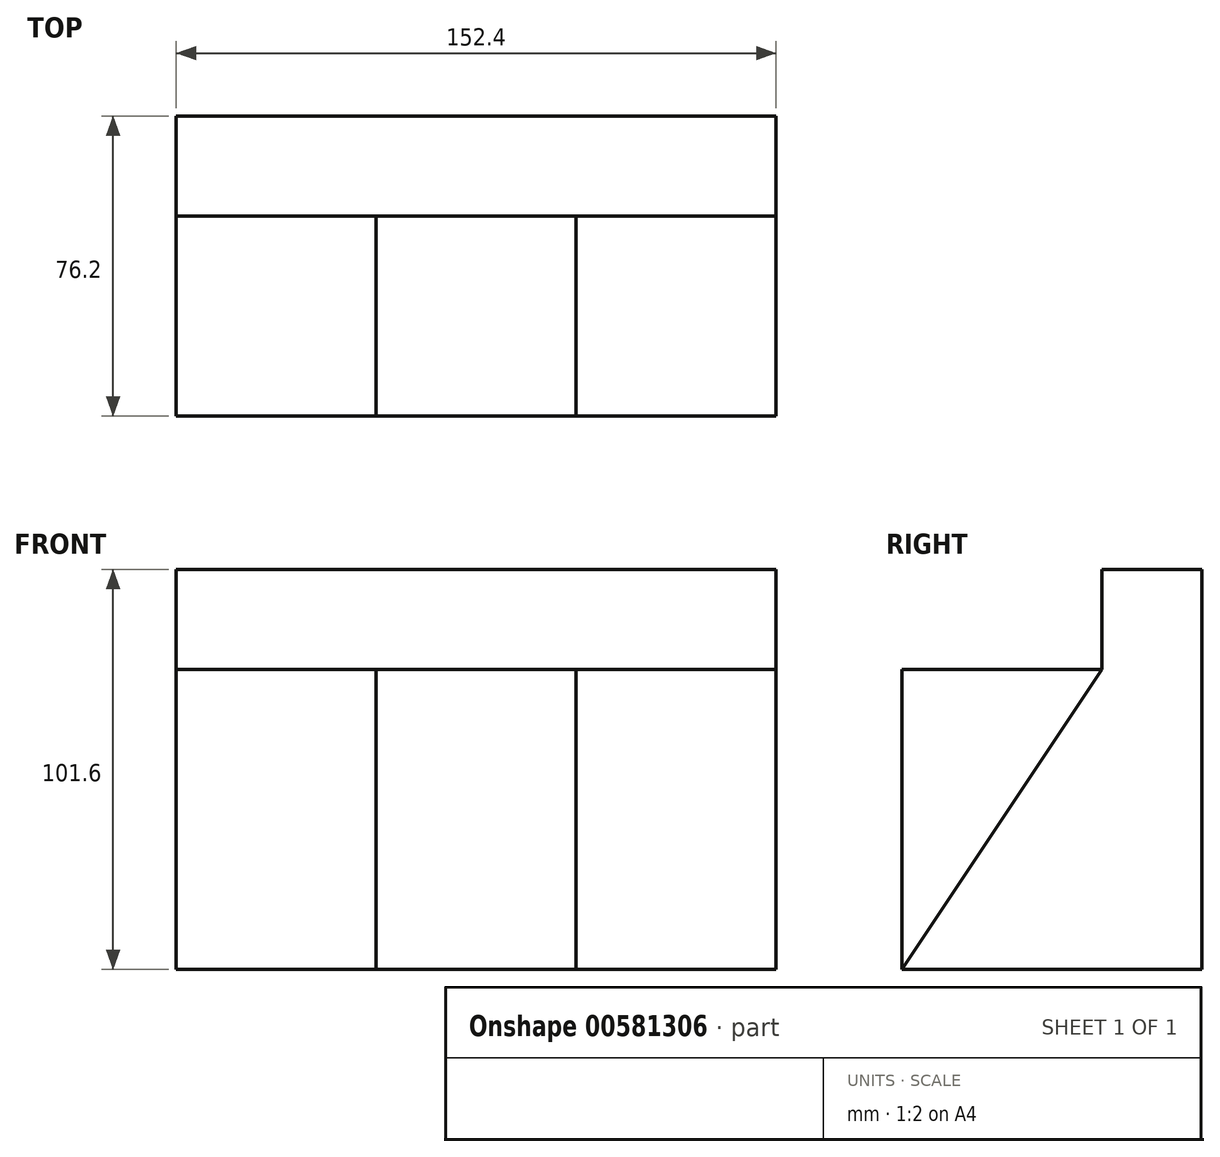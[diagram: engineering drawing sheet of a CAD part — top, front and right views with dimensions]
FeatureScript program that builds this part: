
annotation { "Feature Type Name" : "Feature", "Feature Type Description" : "" }
export const myFeature = defineFeature(function(context is Context, id is Id, definition is map)
    precondition{}
    {
        {
            var Q0;
            Q0=qCreatedBy(makeId("Top.planeOp"),FACE);
            var sketch = newSketch(context, id + "F0", { "sketchPlane" : qUnion([Q0])});
            skLineSegment(sketch, "E0.bottom", {"start": v(-69.4, 16.66) * mm, "end": v(83, 16.66) * mm});
            skLineSegment(sketch, "E0.top", {"start": v(-69.4, -59.54) * mm, "end": v(83, -59.54) * mm});
            skLineSegment(sketch, "E0.left", {"start": v(-69.4, 16.66) * mm, "end": v(-69.4, -59.54) * mm});
            skLineSegment(sketch, "E0.right", {"start": v(83, 16.66) * mm, "end": v(83, -59.54) * mm});
            skSolve(sketch);
        }
        {
            var Q0;
            Q0=makeQuery(id+"F0.imprint","IMPRINT",FACE,{"disambiguationData":[TD([[makeQuery(id+"F0.imprint","IMPRINT",EDGE,{"derivedFrom":sQuery(id+"F0.wireOp",EDGE,"E0.bottom")}),-1.0]])]});
            extrude(context, id + "F1", {"entities" : qUnion([Q0]), "depth" : 101.6 * mm, "offsetDistance" : 25.4 * mm});
        }
        {
            var Q0;
            Q0=makeQuery(id+"F1.opExtrude","SWEPT_FACE",FACE,{"disambiguationData":[OSD([sQuery(id+"F0.wireOp",EDGE,"E0.right")])]});
            var sketch = newSketch(context, id + "F2", { "sketchPlane" : qUnion([Q0])});
            skLineSegment(sketch, "E1.right", {"start": v(16.66, 76.2) * mm, "end": v(16.66, 0) * mm});
            skLineSegment(sketch, "E2.bottom", {"start": v(16.66, 76.2) * mm, "end": v(-8.74, 76.2) * mm});
            skLineSegment(sketch, "E2.top", {"start": v(16.66, 0) * mm, "end": v(-8.74, 0) * mm});
            skLineSegment(sketch, "E2.right", {"start": v(-8.74, 76.2) * mm, "end": v(-8.74, 0) * mm});
            skLineSegment(sketch, "E3", {"start": v(-8.74, 76.2) * mm, "end": v(-59.54, 0) * mm});
            skLineSegment(sketch, "E4.bottom", {"start": v(-8.74, 76.2) * mm, "end": v(16.66, 76.2) * mm});
            skLineSegment(sketch, "E4.top", {"start": v(-8.74, 101.6) * mm, "end": v(16.66, 101.6) * mm});
            skLineSegment(sketch, "E4.left", {"start": v(-8.74, 76.2) * mm, "end": v(-8.74, 101.6) * mm});
            skLineSegment(sketch, "E4.right", {"start": v(16.66, 76.2) * mm, "end": v(16.66, 101.6) * mm});
            skSolve(sketch);
        }
        {
            var Q0;
            Q0=makeQuery(id+"F1.opExtrude","SWEPT_FACE",FACE,{"disambiguationData":[OSD([sQuery(id+"F0.wireOp",EDGE,"E0.top")])]});
            var sketch = newSketch(context, id + "F3", { "sketchPlane" : qUnion([Q0])});
            skLineSegment(sketch, "E5.bottom", {"start": v(-69.4, 76.2) * mm, "end": v(-18.6, 76.2) * mm});
            skLineSegment(sketch, "E5.top", {"start": v(-69.4, 0) * mm, "end": v(-18.6, 0) * mm});
            skLineSegment(sketch, "E5.left", {"start": v(-69.4, 76.2) * mm, "end": v(-69.4, 0) * mm});
            skLineSegment(sketch, "E5.right", {"start": v(-18.6, 76.2) * mm, "end": v(-18.6, 0) * mm});
            skLineSegment(sketch, "E6.bottom", {"start": v(-18.6, 76.2) * mm, "end": v(32.2, 76.2) * mm});
            skLineSegment(sketch, "E6.top", {"start": v(-18.6, 0) * mm, "end": v(32.2, 0) * mm});
            skLineSegment(sketch, "E6.right", {"start": v(32.2, 76.2) * mm, "end": v(32.2, 0) * mm});
            skLineSegment(sketch, "E7.bottom", {"start": v(32.2, 76.2) * mm, "end": v(83, 76.2) * mm});
            skLineSegment(sketch, "E7.top", {"start": v(32.2, 0) * mm, "end": v(83, 0) * mm});
            skLineSegment(sketch, "E7.right", {"start": v(83, 76.2) * mm, "end": v(83, 0) * mm});
            skSolve(sketch);
        }
        {
            var Q0;
            {var subQ4=sQuery(id+"F3.wireOp",EDGE,"E5.bottom");Q0=makeQuery(id+"F3.imprint","IMPRINT",FACE,{"disambiguationData":[TD([[makeQuery(id+"F3.imprint","IMPRINT",EDGE,{"derivedFrom":subQ4}),1.0]])]});}
            extrude(context, id + "F4", {"entities" : qUnion([Q0]), "operationType" : NewBodyOperationType.REMOVE, "oppositeDirection" : true, "depth" : 50.8 * mm, "offsetDistance" : 25.4 * mm});
        }
        {
            var Q0;
            Q0=makeQuery(id+"F2.imprint","IMPRINT",FACE,{"disambiguationData":[TD([[makeQuery(id+"F2.imprint","IMPRINT",EDGE,{"derivedFrom":sQuery(id+"F2.wireOp",EDGE,"E3")}),-1.0]])]});
            extrude(context, id + "F5", {"entities" : qUnion([Q0]), "operationType" : NewBodyOperationType.REMOVE, "oppositeDirection" : true, "depth" : 50.8 * mm, "offsetDistance" : 25.4 * mm});
        }
        {
            var Q0;
            Q0=makeQuery(id+"F1.opExtrude","SWEPT_FACE",FACE,{"disambiguationData":[OSD([sQuery(id+"F0.wireOp",EDGE,"E0.left")])]});
            var sketch = newSketch(context, id + "F6", { "sketchPlane" : qUnion([Q0])});
            skLineSegment(sketch, "E8", {"start": v(8.74, 76.2) * mm, "end": v(59.54, 0) * mm});
            skSolve(sketch);
        }
        {
            var Q0;
            Q0=qSketchRegion(id+"F6",true);
            var Q1;
            Q1=makeQuery(id+"F6.imprint","IMPRINT",FACE,{"disambiguationData":[TD([[makeQuery(id+"F6.imprint","IMPRINT",EDGE,{"derivedFrom":sQuery(id+"F6.wireOp",EDGE,"E8")}),1.0]])]});
            extrude(context, id + "F7", {"entities" : qUnion([Q0, Q1]), "operationType" : NewBodyOperationType.REMOVE, "oppositeDirection" : true, "depth" : 50.8 * mm, "offsetDistance" : 25.4 * mm});
        }
    });
